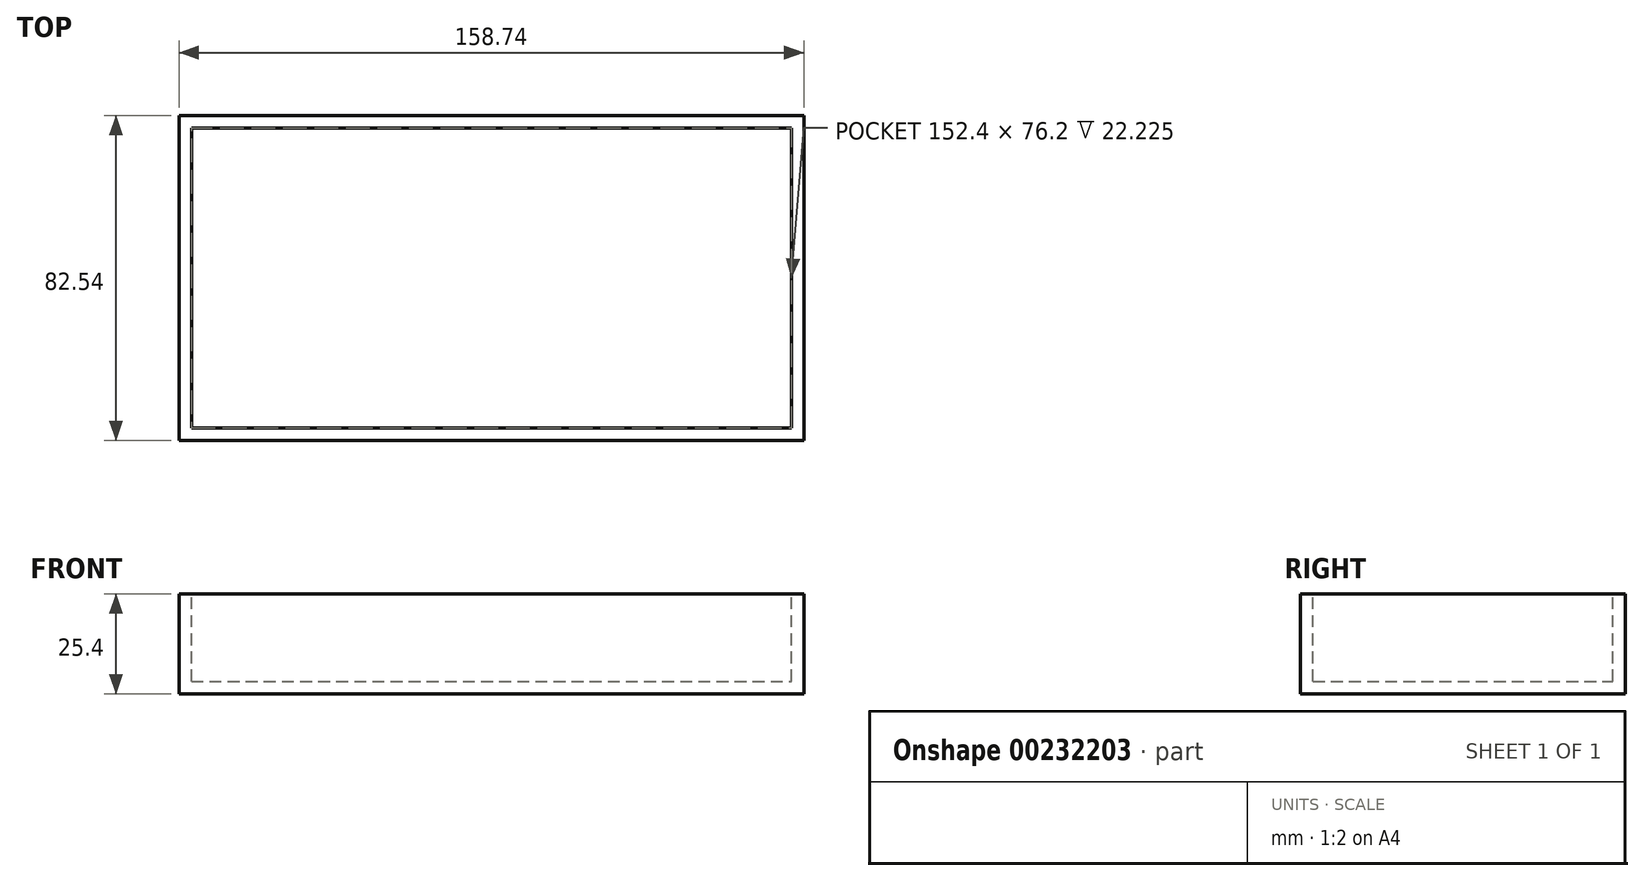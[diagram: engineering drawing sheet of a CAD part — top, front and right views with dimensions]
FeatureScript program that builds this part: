
annotation { "Feature Type Name" : "Feature", "Feature Type Description" : "" }
export const myFeature = defineFeature(function(context is Context, id is Id, definition is map)
    precondition{}
    {
        {
            var Q0;
            Q0=qCreatedBy(makeId("Top.planeOp"),FACE);
            var sketch = newSketch(context, id + "F0", { "sketchPlane" : qUnion([Q0])});
            skLineSegment(sketch, "E0.bottom", {"start": v(79.38, -41.28) * mm, "end": v(-79.37, -41.28) * mm});
            skLineSegment(sketch, "E0.top", {"start": v(79.38, 41.28) * mm, "end": v(-79.38, 41.28) * mm});
            skLineSegment(sketch, "E0.left", {"start": v(79.38, -41.28) * mm, "end": v(79.38, 41.28) * mm});
            skLineSegment(sketch, "E0.right", {"start": v(-79.37, -41.28) * mm, "end": v(-79.38, 41.28) * mm});
            skPoint(sketch, "E0.middle", {"position": v(0, 0) * mm});
            skSolve(sketch);
        }
        {
            var Q0;
            Q0 = qSketchRegion(id + "F0", true);
            extrude(context, id + "F1", {"entities" : qUnion([Q0]), "depth" : 25.4 * mm});
        }
        {
            var Q0;
            Q0=qCreatedBy(makeId("Top.planeOp"),FACE);
            var sketch = newSketch(context, id + "F2", { "sketchPlane" : qUnion([Q0])});
            skLineSegment(sketch, "E1.bottom", {"start": v(76.2, -38.1) * mm, "end": v(-76.2, -38.1) * mm});
            skLineSegment(sketch, "E1.top", {"start": v(76.2, 38.1) * mm, "end": v(-76.2, 38.1) * mm});
            skLineSegment(sketch, "E1.left", {"start": v(76.2, -38.1) * mm, "end": v(76.2, 38.1) * mm});
            skLineSegment(sketch, "E1.right", {"start": v(-76.2, -38.1) * mm, "end": v(-76.2, 38.1) * mm});
            skPoint(sketch, "E1.middle", {"position": v(0, 0) * mm});
            skSolve(sketch);
        }
        {
            var Q0;
            Q0 = qSketchRegion(id + "F2", true);
            extrude(context, id + "F3", {"entities" : qUnion([Q0]), "operationType" : NewBodyOperationType.REMOVE, "depth" : 22.22 * mm});
        }
        {
            var Q0;
            Q0=makeQuery(id+"F1.opExtrude","SWEPT_BODY",BODY,{"disambiguationData":[OSD([sQuery(id+"F0.wireOp",EDGE,"E0.bottom"),sQuery(id+"F0.wireOp",EDGE,"E0.top"),sQuery(id+"F0.wireOp",EDGE,"E0.left"),sQuery(id+"F0.wireOp",EDGE,"E0.right")])]});
            var Q1;
            Q1=makeQuery(id+"F1.opExtrude","CAP_EDGE",EDGE,{"disambiguationData":[OSD([sQuery(id+"F0.wireOp",EDGE,"E0.left")])],"isStart":true});
            transform(context, id + "F4", {"entities" : qUnion([Q0]), "transformType" : TransformType.ROTATION, "transformAxis" : qUnion([Q1]), "angle" : 180 * degree, "makeCopy" : false});
        }
    });
